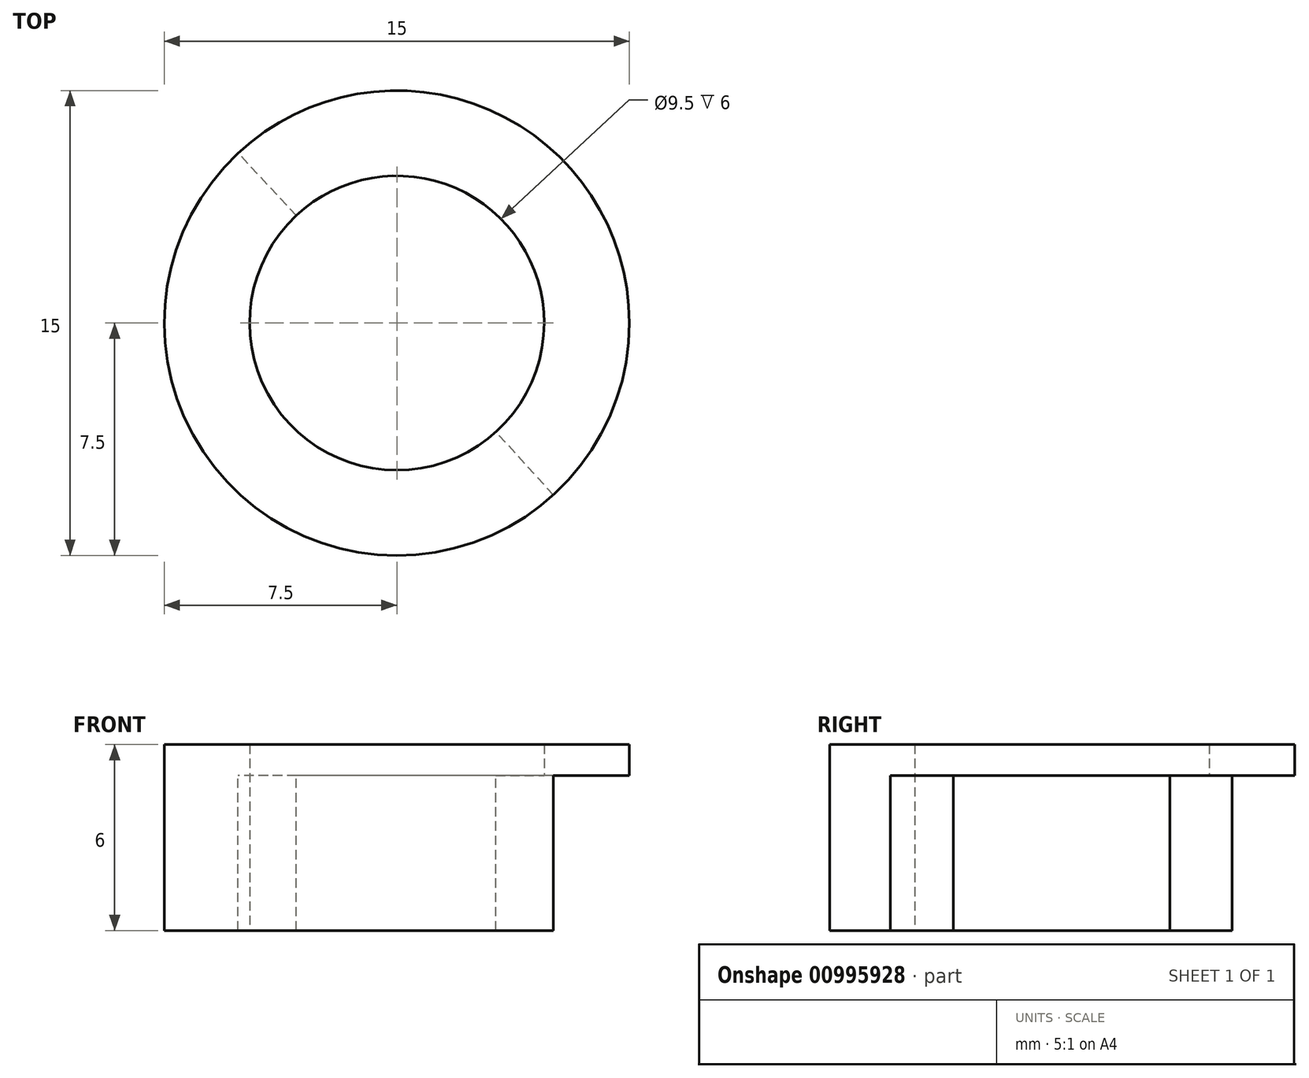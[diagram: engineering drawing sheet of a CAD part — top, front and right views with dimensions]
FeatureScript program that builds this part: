
annotation { "Feature Type Name" : "Feature", "Feature Type Description" : "" }
export const myFeature = defineFeature(function(context is Context, id is Id, definition is map)
    precondition{}
    {
        {
            var Q0;
            Q0=qCreatedBy(makeId("Top.planeOp"),FACE);
            var sketch = newSketch(context, id + "F0", { "sketchPlane" : qUnion([Q0])});
            skCircle(sketch, "E0", {"center": v(0, 0) * mm, "radius": 7.5 * mm});
            skCircle(sketch, "E1", {"center": v(0, 0) * mm, "radius": 4.75 * mm});
            skSolve(sketch);
        }
        {
            var Q0;
            Q0=makeQuery(id+"F0.imprint","IMPRINT",FACE,{"disambiguationData":[TD([[makeQuery(id+"F0.imprint","IMPRINT",EDGE,{"derivedFrom":sQuery(id+"F0.wireOp",EDGE,"E0")}),1.0]])]});
            extrude(context, id + "F1", {"entities" : qUnion([Q0]), "depth" : 1 * mm, "offsetDistance" : 25 * mm});
        }
        {
            var Q0;
            Q0=makeQuery(id+"F1.opExtrude","CAP_FACE",FACE,{"disambiguationData":[OSD([sQuery(id+"F0.wireOp",EDGE,"E0"),sQuery(id+"F0.wireOp",EDGE,"E1")])],"isStart":true});
            var sketch = newSketch(context, id + "F2", { "sketchPlane" : qUnion([Q0])});
            skCircle(sketch, "E2.0.0", {"center": v(0, 0) * mm, "radius": 7.5 * mm});
            skLineSegment(sketch, "E3", {"start": v(5.05, 5.55) * mm, "end": v(0, 0) * mm});
            skLineSegment(sketch, "E4", {"start": v(0, 0) * mm, "end": v(-5.12, -5.48) * mm});
            skSolve(sketch);
        }
        {
            var Q0;
            {var subQ0=sQuery(id+"F2.wireOp",EDGE,"E3");var subQ1=sQuery(id+"F2.wireOp",EDGE,"E2.0.0");var subQ2=makeQuery(id+"F2.imprint","INTERSECT",VERTEX,{"derivedFrom":[subQ1,subQ0]});Q0=makeQuery(id+"F2.imprint","IMPRINT",FACE,{"disambiguationData":[TD([[makeQuery(id+"F2.imprint","IMPRINT",EDGE,{"disambiguationData":[TD([[subQ2,1.0]])],"derivedFrom":subQ1}),-1.0]])]});}
            extrude(context, id + "F3", {"entities" : qUnion([Q0]), "operationType" : NewBodyOperationType.ADD, "depth" : 5 * mm, "offsetDistance" : 25 * mm});
        }
    });
